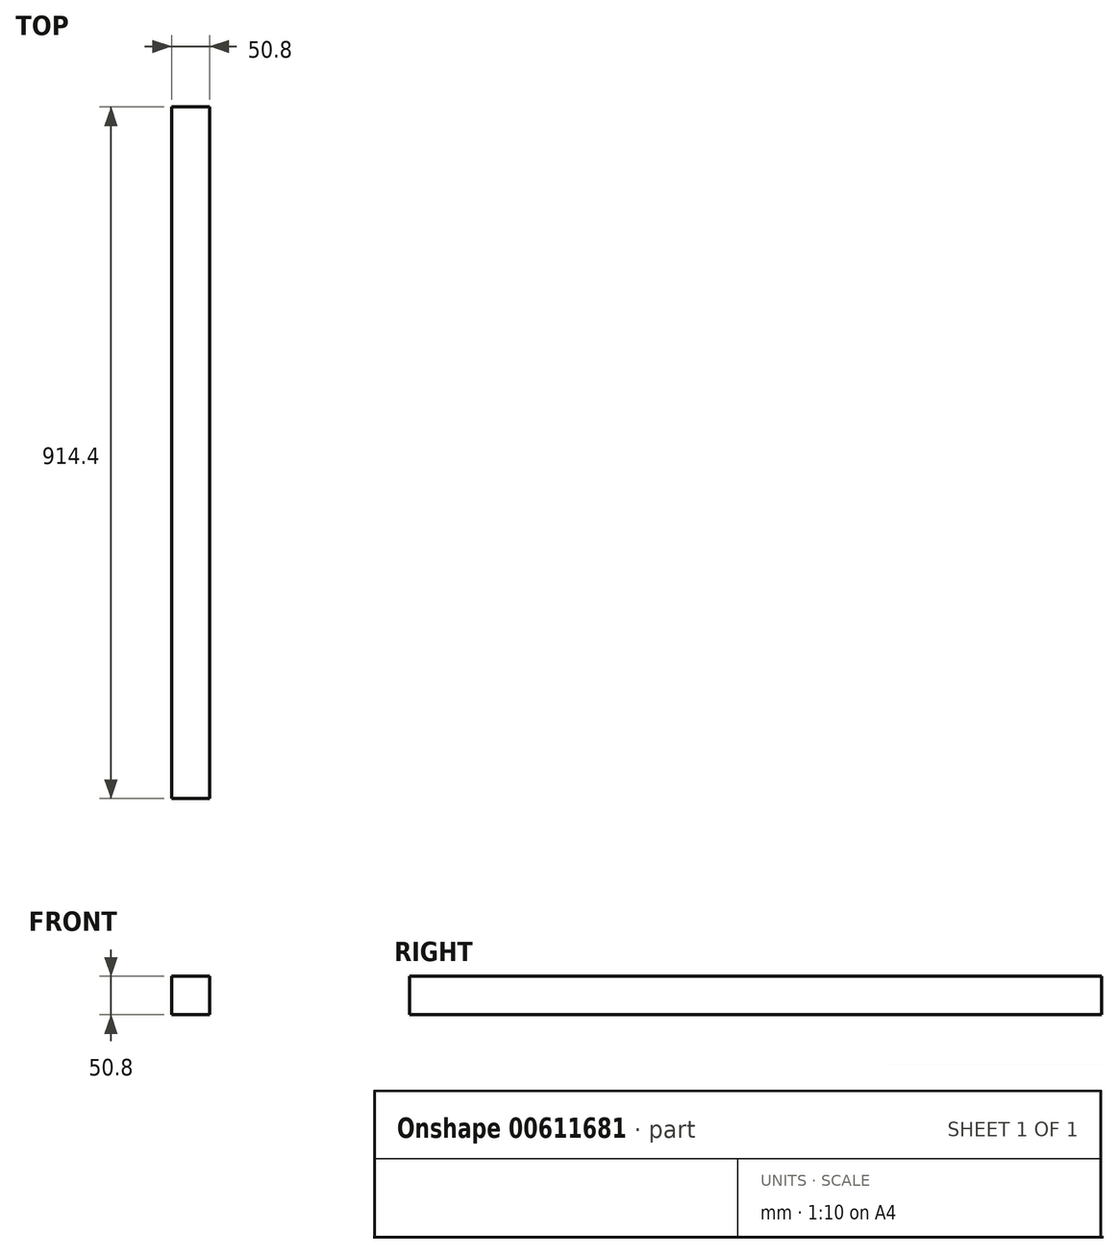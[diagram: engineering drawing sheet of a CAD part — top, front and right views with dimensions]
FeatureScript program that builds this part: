
annotation { "Feature Type Name" : "Feature", "Feature Type Description" : "" }
export const myFeature = defineFeature(function(context is Context, id is Id, definition is map)
    precondition{}
    {
        {
            var Q0;
            Q0=qCreatedBy(makeId("Front.planeOp"),FACE);
            var sketch = newSketch(context, id + "F0", { "sketchPlane" : qUnion([Q0])});
            skLineSegment(sketch, "E0.bottom", {"start": v(-25.4, 25.4) * mm, "end": v(25.4, 25.4) * mm});
            skLineSegment(sketch, "E0.top", {"start": v(-25.4, -25.4) * mm, "end": v(25.4, -25.4) * mm});
            skLineSegment(sketch, "E0.left", {"start": v(-25.4, 25.4) * mm, "end": v(-25.4, -25.4) * mm});
            skLineSegment(sketch, "E0.right", {"start": v(25.4, 25.4) * mm, "end": v(25.4, -25.4) * mm});
            skSolve(sketch);
        }
        {
            var Q0;
            Q0=makeQuery(id+"F0.imprint","IMPRINT",FACE,{"disambiguationData":[TD([[makeQuery(id+"F0.imprint","IMPRINT",EDGE,{"derivedFrom":sQuery(id+"F0.wireOp",EDGE,"E0.bottom")}),-1.0]])]});
            extrude(context, id + "F1", {"entities" : qUnion([Q0]), "depth" : 457.2 * mm, "offsetDistance" : 25.4 * mm, "hasSecondDirection" : true, "secondDirectionOppositeDirection" : true, "secondDirectionDepth" : 457.2 * mm});
        }
    });
